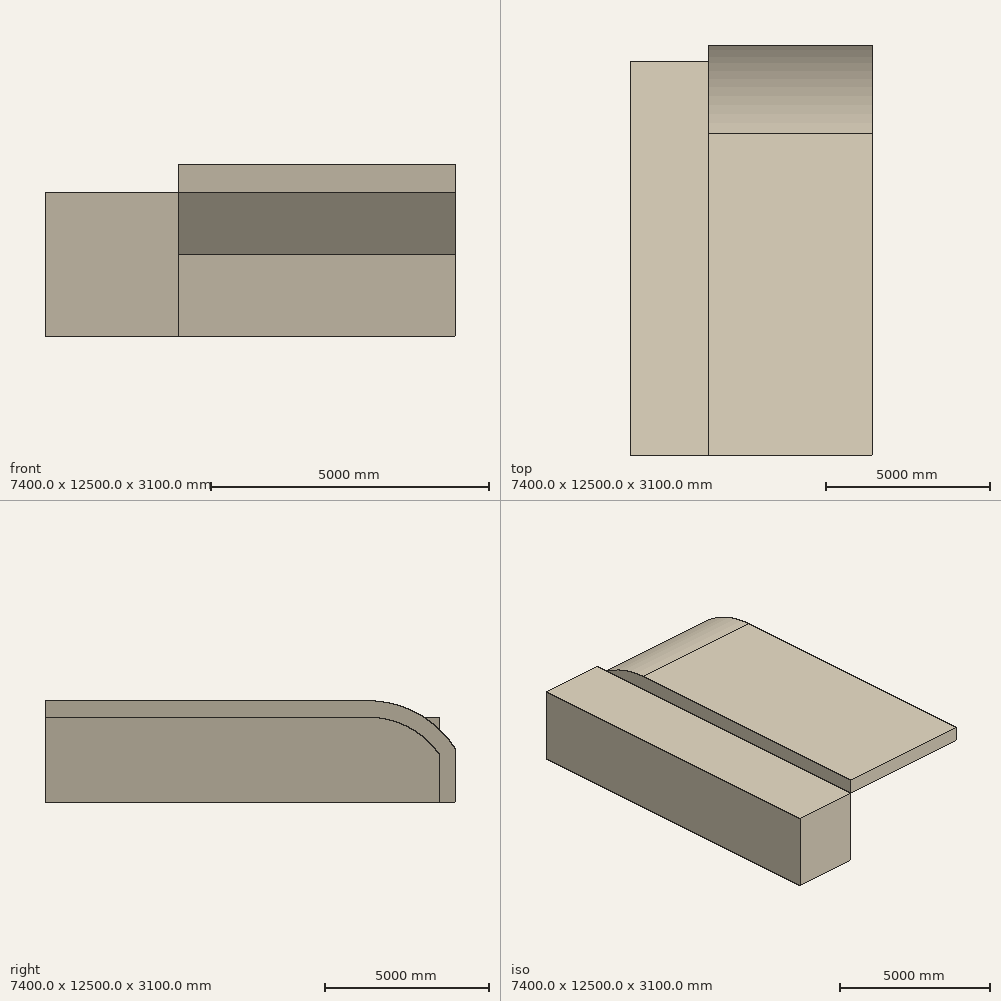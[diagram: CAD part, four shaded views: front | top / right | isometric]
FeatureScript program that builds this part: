
annotation { "Feature Type Name" : "Feature", "Feature Type Description" : "" }
export const myFeature = defineFeature(function(context is Context, id is Id, definition is map)
    precondition{}
    {
        {
            var Q0;
            Q0=qCreatedBy(makeId("Front.planeOp"),FACE);
            var sketch = newSketch(context, id + "F0", { "sketchPlane" : qUnion([Q0])});
            skLineSegment(sketch, "E0.rect.bottom", {"start": v(1200, -1300) * mm, "end": v(-1200, -1300) * mm});
            skLineSegment(sketch, "E0.rect.top", {"start": v(1200, 1300) * mm, "end": v(-1200, 1300) * mm});
            skLineSegment(sketch, "E0.rect.left", {"start": v(1200, -1300) * mm, "end": v(1200, 1300) * mm});
            skLineSegment(sketch, "E0.rect.right", {"start": v(-1200, -1300) * mm, "end": v(-1200, 1300) * mm});
            skPoint(sketch, "E0.rect.middle", {"position": v(0, 0) * mm});
            skSolve(sketch);
        }
        {
            var Q0;
            Q0 = qSketchRegion(id + "F0", true);
            extrude(context, id + "F1", {"entities" : qUnion([Q0]), "oppositeDirection" : true, "depth" : 12000 * mm});
        }
        {
            var Q0;
            Q0=makeQuery(id+"F1.opExtrude","SWEPT_FACE",FACE,{"disambiguationData":[OSD([sQuery(id+"F0.wireOp",EDGE,"E0.rect.left")])]});
            var sketch = newSketch(context, id + "F2", { "sketchPlane" : qUnion([Q0])});
            skLineSegment(sketch, "E1", {"start": v(0, 1300) * mm, "end": v(9825.05, 1300) * mm});
            skLineSegment(sketch, "E2", {"start": v(12000, -1300) * mm, "end": v(12000, 173.87) * mm});
            skArc(sketch, "E3", {"start": v(12000, 173.87) * mm, "mid": v(11049.65, 1001.77) * mm, "end": v(9825.05, 1300) * mm});
            skLineSegment(sketch, "E4.0", {"start": v(12500, -1300) * mm, "end": v(12500, 325.27) * mm});
            skArc(sketch, "E4.1", {"start": v(12500, 325.27) * mm, "mid": v(11352.32, 1406.9) * mm, "end": v(9825.05, 1800) * mm});
            skLineSegment(sketch, "E4.2", {"start": v(0, 1800) * mm, "end": v(9825.05, 1800) * mm});
            skLineSegment(sketch, "E5", {"start": v(0, 1800) * mm, "end": v(0, 1300) * mm});
            skLineSegment(sketch, "E6", {"start": v(12000, -1300) * mm, "end": v(12500, -1300) * mm});
            skSolve(sketch);
        }
        {
            var Q0;
            Q0 = qSketchRegion(id + "F2", true);
            extrude(context, id + "F3", {"entities" : qUnion([Q0]), "depth" : 5000 * mm});
        }
    });
